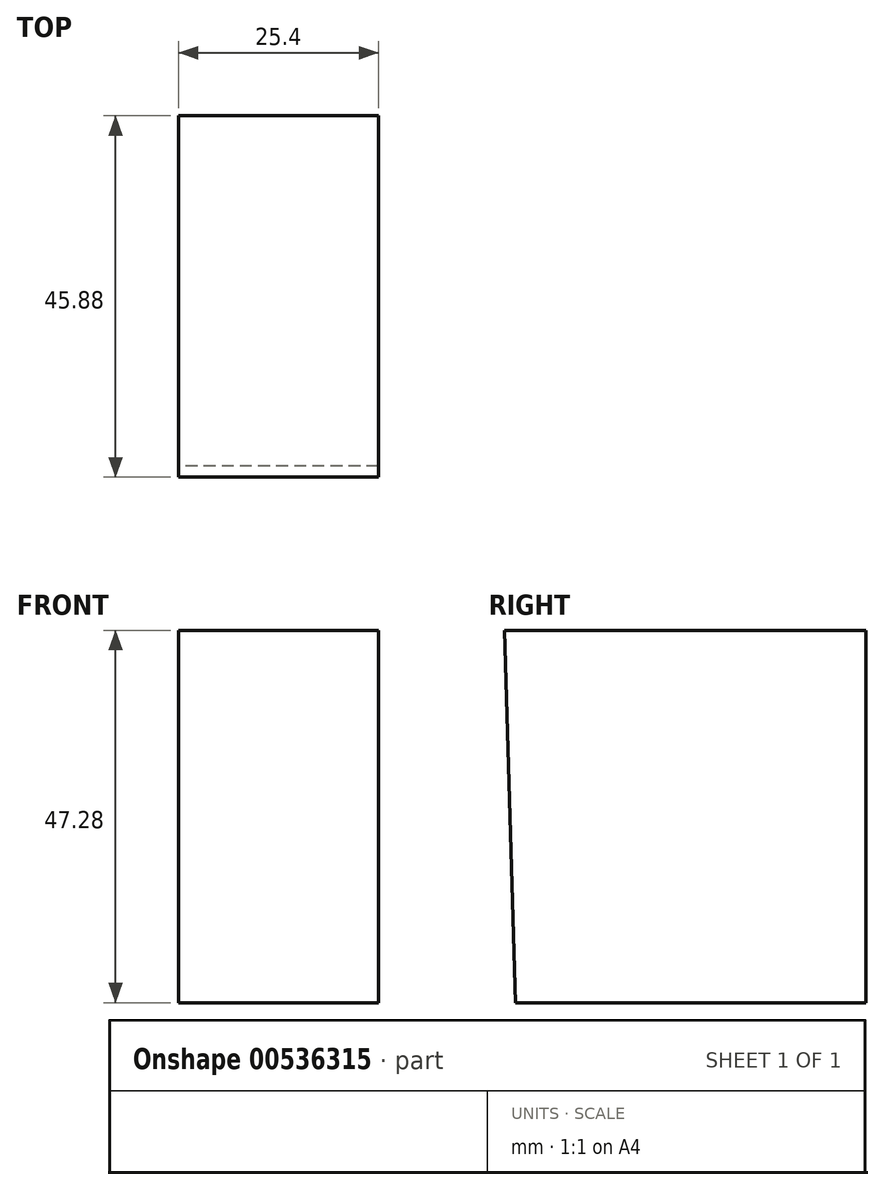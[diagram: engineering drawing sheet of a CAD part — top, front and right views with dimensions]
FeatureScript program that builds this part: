
annotation { "Feature Type Name" : "Feature", "Feature Type Description" : "" }
export const myFeature = defineFeature(function(context is Context, id is Id, definition is map)
    precondition{}
    {
        {
            var Q0;
            Q0=qCreatedBy(makeId("Right.planeOp"),FACE);
            var sketch = newSketch(context, id + "F0", { "sketchPlane" : qUnion([Q0])});
            skLineSegment(sketch, "E0", {"start": v(-35.53, 47.28) * mm, "end": v(10.35, 47.28) * mm});
            skLineSegment(sketch, "E1", {"start": v(10.35, 47.28) * mm, "end": v(10.35, 0) * mm});
            skLineSegment(sketch, "E2", {"start": v(10.35, 0) * mm, "end": v(-34.13, 0) * mm});
            skLineSegment(sketch, "E3", {"start": v(-35.53, 47.28) * mm, "end": v(-34.13, 0) * mm});
            skSolve(sketch);
        }
        {
            var Q0;
            Q0=makeQuery(id+"F0.imprint","IMPRINT",FACE,{"disambiguationData":[TD([[makeQuery(id+"F0.imprint","IMPRINT",EDGE,{"derivedFrom":sQuery(id+"F0.wireOp",EDGE,"E0")}),-1.0]])]});
            extrude(context, id + "F1", {"entities" : qUnion([Q0]), "depth" : 25.4 * mm, "offsetDistance" : 25.4 * mm});
        }
    });
